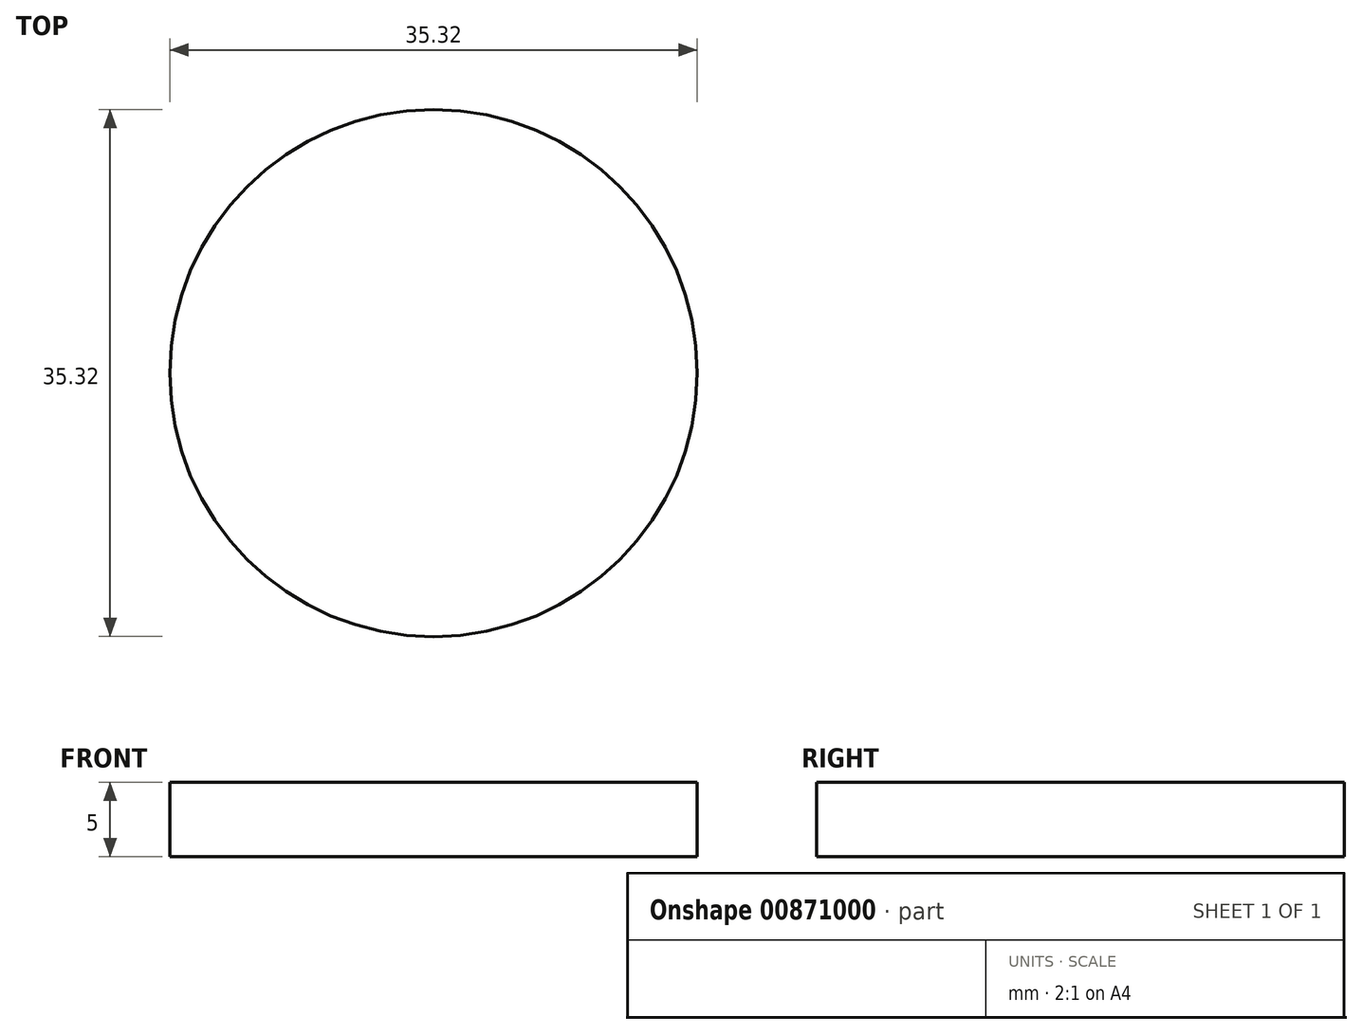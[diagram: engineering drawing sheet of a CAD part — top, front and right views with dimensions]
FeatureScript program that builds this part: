
annotation { "Feature Type Name" : "Feature", "Feature Type Description" : "" }
export const myFeature = defineFeature(function(context is Context, id is Id, definition is map)
    precondition{}
    {
        {
            var Q0;
            Q0=qCreatedBy(makeId("Top.planeOp"),FACE);
            var sketch = newSketch(context, id + "F0", { "sketchPlane" : qUnion([Q0])});
            skCircle(sketch, "E0", {"center": v(0, 0) * mm, "radius": 17.66 * mm});
            skSolve(sketch);
        }
        {
            var Q0;
            Q0 = qSketchRegion(id + "F0", true);
            extrude(context, id + "F1", {"entities" : qUnion([Q0]), "depth" : 5 * mm, "offsetDistance" : 25 * mm});
        }
    });
